# Revit family: Light_Shelf-Corner-Kawneer-InLighten
name_source: partatom
category: Specialty Equipment
revit_build: Autodesk Revit 2015 (Build: 20140905_0730(x64)
units: mm (PartAtom-declared; Revit-internal decimal feet)

## types (3) — shared parameters
Bracket Material = Aluminum Composite - Kawneer - Bone White
Default Elevation = 4' - 0"
Description = Light Shelf 90 Degree Corner
Manufacturer = Kawneer
Model = InLighten
OmniClass Number = 23.25.20.14.11.11
OmniClass Title = Curtain Wall Components
Product Documentation Link = http://www.kawneer.com
Product Page URL = http://www.kawneer.com
Product data url = https://bimobject.com
Trim Finish = Aluminum Composite - Kawneer - Bone White
URL = http://www.kawneer.com

## per-type parameters (varying)
| type | Panel Finish | Panel Type | Type Comments |
| 16mm Multi-Layer-Extruded-Polycarbonate-Sheet Corner | Polycarbonate - Kawneer - 16 mm - Ice | Shelf-Kawneer-16mm_Multi-Layer-Extruded-Polycarbonate-Sheet_Corner : 16 mm | 16mm Multi Layer Extruded Polycarbonate |
| 4mm Reynobond-ACM Panel Corner | Aluminum Composite - Kawneer - Bone White | Shelf-Kawneer-4mm_Reynobond-ACM Panel_Corner : 4 mm | 4 mm Reynobond ACM Panel |
| 4mm Monolithic-Polycarbonate-Sheet Corner | Polycarbonate - Kawneer - 4 mm - Ice | Shelf-Kawneer-4mm_Monolithic-Polycarbonate-Sheet_Corner : 4 mm | 4mm Monolithic Polycarbonate |

## geometry (parser evidence)
native form markers: Sweep x17
no freeform markers — native parametric forms only
